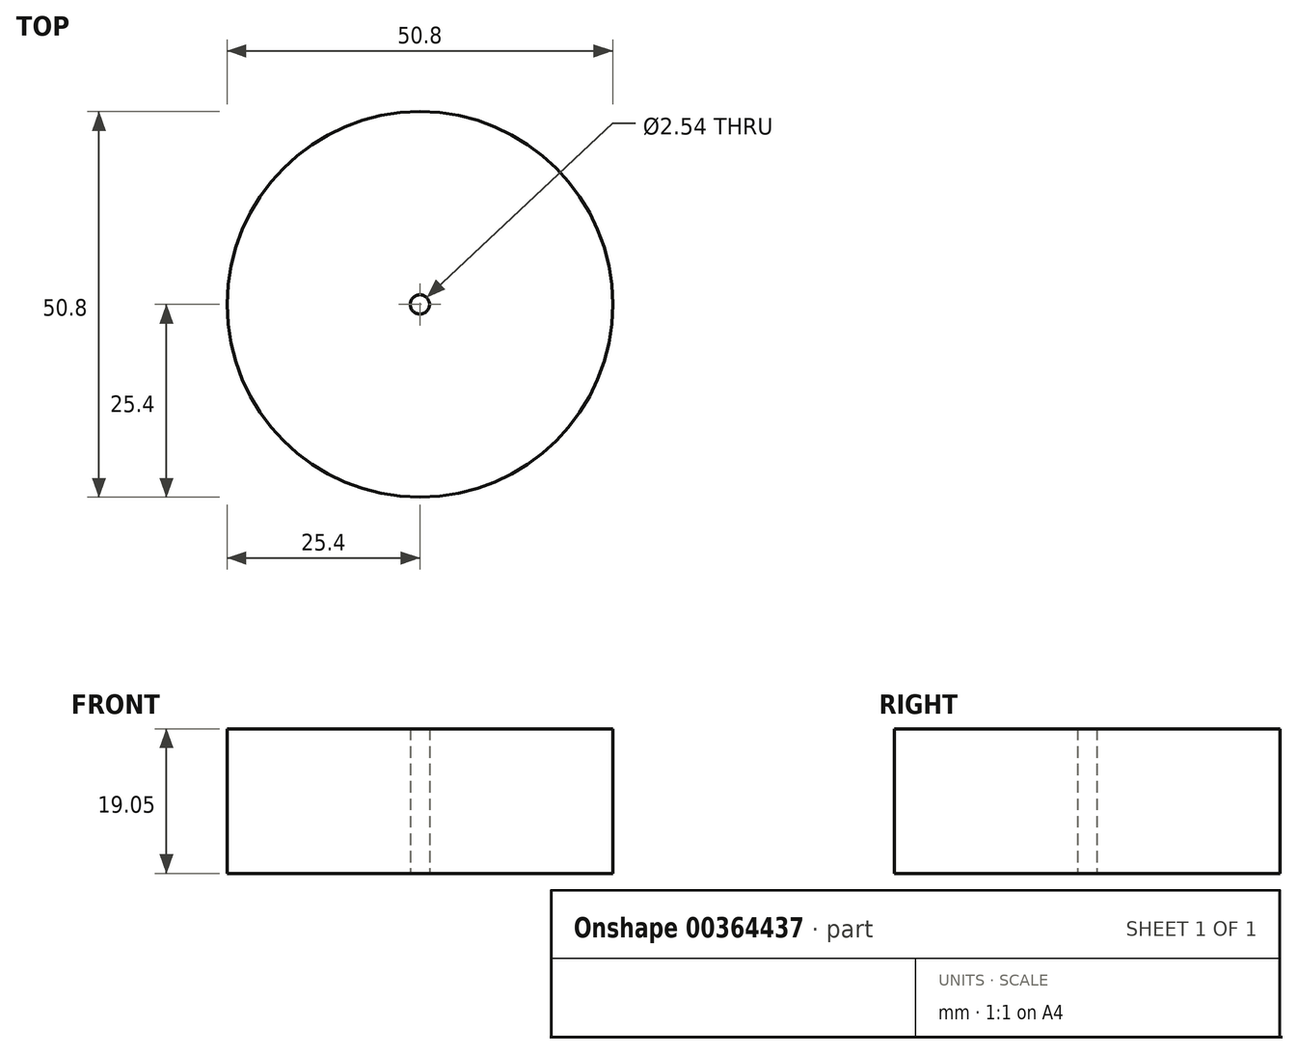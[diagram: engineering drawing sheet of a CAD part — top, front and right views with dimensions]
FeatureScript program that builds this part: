
annotation { "Feature Type Name" : "Feature", "Feature Type Description" : "" }
export const myFeature = defineFeature(function(context is Context, id is Id, definition is map)
    precondition{}
    {
        {
            var Q0;
            Q0=qCreatedBy(makeId("Top.planeOp"),FACE);
            var sketch = newSketch(context, id + "F0", { "sketchPlane" : qUnion([Q0])});
            skCircle(sketch, "E0", {"center": v(0, 0) * mm, "radius": 25.4 * mm});
            skCircle(sketch, "E1", {"center": v(0, 0) * mm, "radius": 1.27 * mm});
            skSolve(sketch);
        }
        {
            var Q0;
            Q0=makeQuery(id+"F0.imprint","IMPRINT",FACE,{"disambiguationData":[TD([[makeQuery(id+"F0.imprint","IMPRINT",EDGE,{"derivedFrom":sQuery(id+"F0.wireOp",EDGE,"E0")}),1.0]])]});
            extrude(context, id + "F1", {"entities" : qUnion([Q0]), "depth" : 19.05 * mm});
        }
    });
